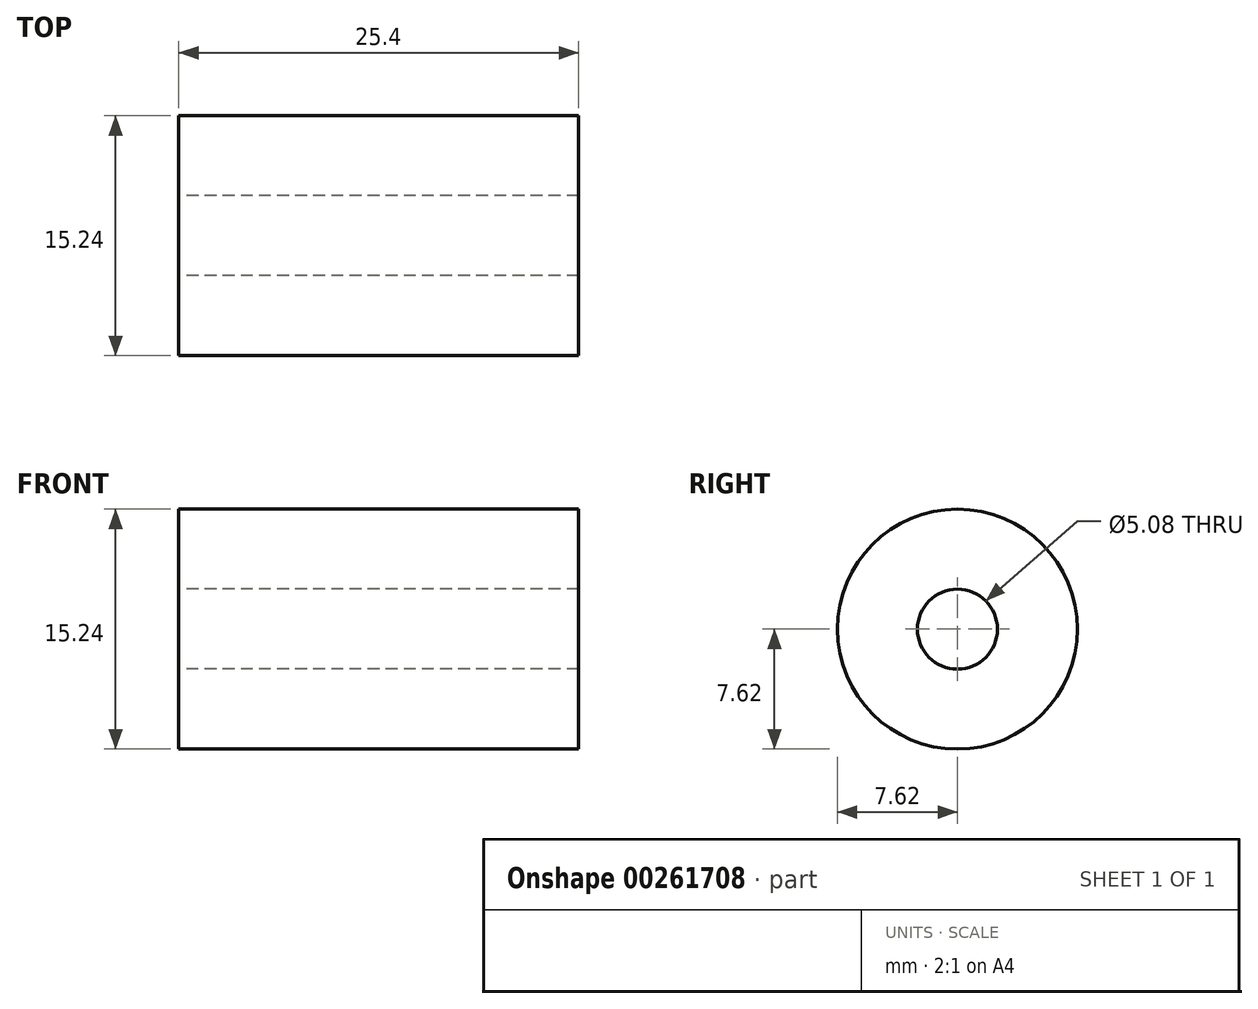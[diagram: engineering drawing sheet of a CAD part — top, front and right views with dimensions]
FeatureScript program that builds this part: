
annotation { "Feature Type Name" : "Feature", "Feature Type Description" : "" }
export const myFeature = defineFeature(function(context is Context, id is Id, definition is map)
    precondition{}
    {
        {
            var Q0;
            Q0=qCreatedBy(makeId("Right.planeOp"),FACE);
            var sketch = newSketch(context, id + "F0", { "sketchPlane" : qUnion([Q0])});
            skCircle(sketch, "E0", {"center": v(0, 0) * mm, "radius": 7.62 * mm});
            skCircle(sketch, "E1", {"center": v(0, 0) * mm, "radius": 2.54 * mm});
            skSolve(sketch);
        }
        {
            var Q0;
            Q0 = qSketchRegion(id + "F0", true);
            extrude(context, id + "F1", {"entities" : qUnion([Q0]), "depth" : 25.4 * mm});
        }
    });
